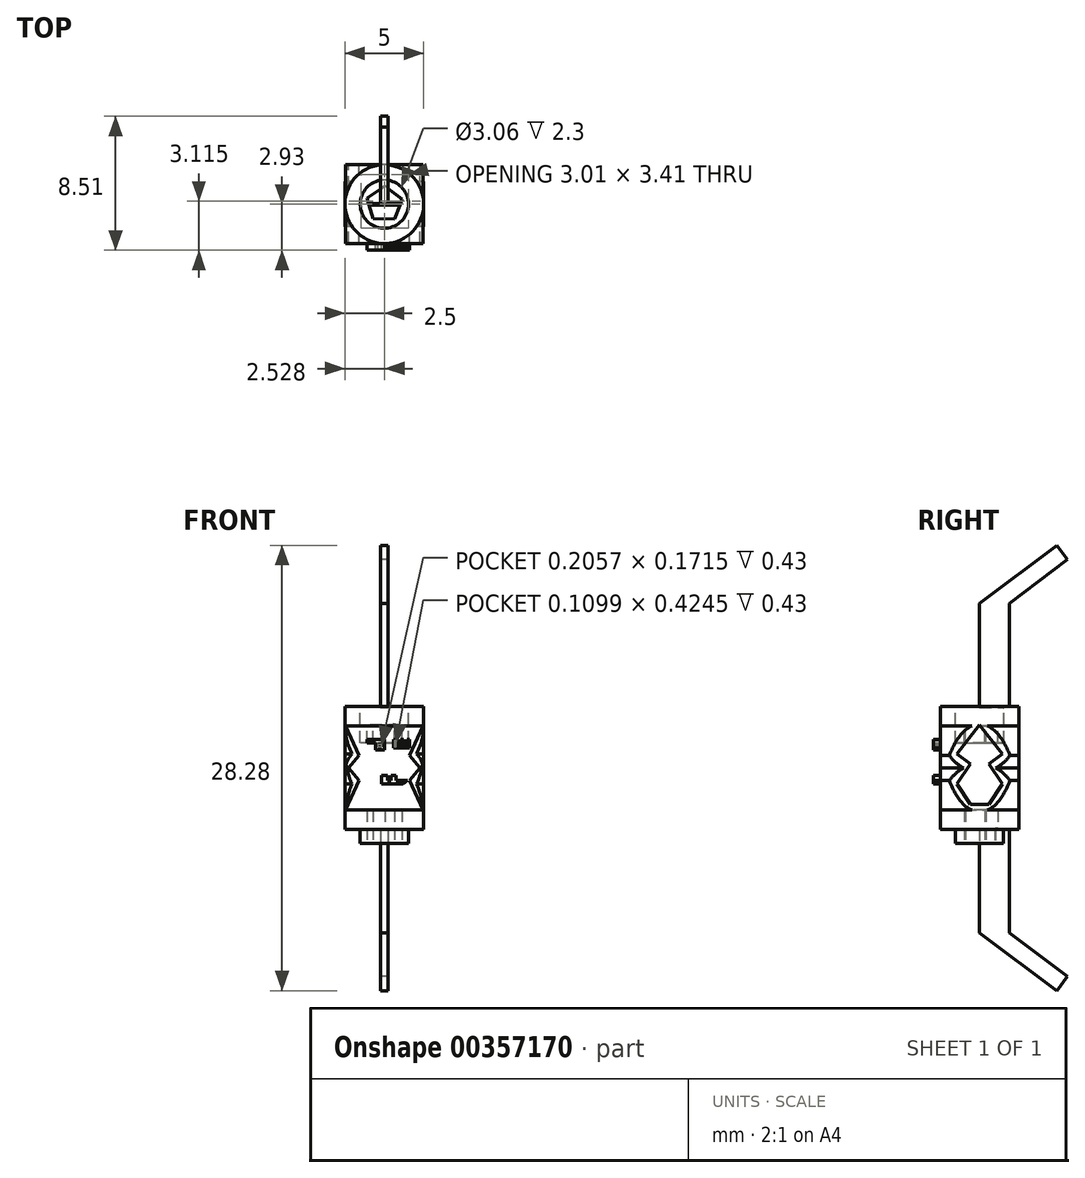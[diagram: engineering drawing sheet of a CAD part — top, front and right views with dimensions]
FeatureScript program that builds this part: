
annotation { "Feature Type Name" : "Feature", "Feature Type Description" : "" }
export const myFeature = defineFeature(function(context is Context, id is Id, definition is map)
    precondition{}
    {
        {
            var Q0;
            Q0=qCreatedBy(makeId("Top.planeOp"),FACE);
            var sketch = newSketch(context, id + "F0", { "sketchPlane" : qUnion([Q0])});
            skCircle(sketch, "E0", {"center": v(0, 0) * mm, "radius": 2.5 * mm});
            skCircle(sketch, "E1", {"center": v(0, 0) * mm, "radius": 1.53 * mm});
            skCircle(sketch, "E2.cCircle", {"center": v(0, 0) * mm, "radius": 0.94 * mm, "construction": true});
            skLineSegment(sketch, "E2.0", {"start": v(1.12, 0.32) * mm, "end": v(0.65, -0.96) * mm});
            skLineSegment(sketch, "E2.1", {"start": v(0.65, -0.96) * mm, "end": v(-0.72, -0.92) * mm});
            skLineSegment(sketch, "E2.2", {"start": v(-0.72, -0.92) * mm, "end": v(-1.1, 0.4) * mm});
            skLineSegment(sketch, "E2.3", {"start": v(-1.1, 0.4) * mm, "end": v(0.04, 1.16) * mm});
            skLineSegment(sketch, "E2.4", {"start": v(0.04, 1.16) * mm, "end": v(1.12, 0.32) * mm});
            skPoint(sketch, "E2.0.midPoint", {"position": v(0.88, -0.32) * mm});
            skSolve(sketch);
        }
        {
            var Q0;
            Q0=makeQuery(id+"F0.imprint","IMPRINT",FACE,{"disambiguationData":[TD([[makeQuery(id+"F0.imprint","IMPRINT",EDGE,{"derivedFrom":sQuery(id+"F0.wireOp",EDGE,"E1")}),1.0]])]});
            extrude(context, id + "F1", {"entities" : qUnion([Q0]), "endBound" : BoundingType.SYMMETRIC, "depth" : 9.6 * mm});
        }
        {
            var Q0;
            Q0=makeQuery(id+"F0.imprint","IMPRINT",FACE,{"disambiguationData":[TD([[makeQuery(id+"F0.imprint","IMPRINT",EDGE,{"derivedFrom":sQuery(id+"F0.wireOp",EDGE,"E0")}),1.0]])]});
            extrude(context, id + "F2", {"entities" : qUnion([Q0]), "operationType" : NewBodyOperationType.ADD, "endBound" : BoundingType.SYMMETRIC, "depth" : 7.8 * mm});
        }
        {
            var Q0;
            Q0=qCreatedBy(makeId("Front.planeOp"),FACE);
            var sketch = newSketch(context, id + "F3", { "sketchPlane" : qUnion([Q0])});
            skLineSegment(sketch, "E3", {"start": v(0, 2.67) * mm, "end": v(2.28, 0) * mm});
            skLineSegment(sketch, "E4", {"start": v(2.28, 0) * mm, "end": v(0, -2.67) * mm});
            skLineSegment(sketch, "E5", {"start": v(1.6, -0.8) * mm, "end": v(2.45, -2.67) * mm});
            skLineSegment(sketch, "E6", {"start": v(2.45, -2.67) * mm, "end": v(0, -2.67) * mm});
            skLineSegment(sketch, "E7.MirrorCS", {"start": v(1.6, 0.8) * mm, "end": v(2.45, 2.67) * mm});
            skLineSegment(sketch, "E8.MirrorCS", {"start": v(2.45, 2.67) * mm, "end": v(0, 2.67) * mm});
            skLineSegment(sketch, "E9", {"start": v(1.6, 0.8) * mm, "end": v(1.6, -0.8) * mm});
            skLineSegment(sketch, "E10.MirrorCS", {"start": v(-2.45, 2.67) * mm, "end": v(0, 2.67) * mm});
            skLineSegment(sketch, "E11.MirrorCS", {"start": v(0, 2.67) * mm, "end": v(-2.28, 0) * mm});
            skLineSegment(sketch, "E12.MirrorCS", {"start": v(-1.6, 0.8) * mm, "end": v(-2.45, 2.67) * mm});
            skLineSegment(sketch, "E13.MirrorCS", {"start": v(-1.6, 0.8) * mm, "end": v(-1.6, -0.8) * mm});
            skLineSegment(sketch, "E14.MirrorCS", {"start": v(-2.28, 0) * mm, "end": v(0, -2.67) * mm});
            skLineSegment(sketch, "E15.MirrorCS", {"start": v(-1.6, -0.8) * mm, "end": v(-2.45, -2.67) * mm});
            skLineSegment(sketch, "E16.MirrorCS", {"start": v(-2.45, -2.67) * mm, "end": v(0, -2.67) * mm});
            skLineSegment(sketch, "E17", {"start": v(1.6, 0) * mm, "end": v(-1.6, 0) * mm});
            skLineSegment(sketch, "E18", {"start": v(0, 2.67) * mm, "end": v(0, -2.67) * mm});
            skSolve(sketch);
        }
        {
            var Q0;
            Q0 = qSketchRegion(id + "F3", true);
            extrude(context, id + "F4", {"entities" : qUnion([Q0]), "operationType" : NewBodyOperationType.ADD, "endBound" : BoundingType.SYMMETRIC, "depth" : 5 * mm});
        }
        {
            var Q0;
            Q0=qCreatedBy(makeId("Right.planeOp"),FACE);
            var sketch = newSketch(context, id + "F5", { "sketchPlane" : qUnion([Q0])});
            skLineSegment(sketch, "E19", {"start": v(0, 2.74) * mm, "end": v(1.44, 0.9) * mm});
            skLineSegment(sketch, "E20", {"start": v(1.44, 0.9) * mm, "end": v(0.6, 0.25) * mm});
            skLineSegment(sketch, "E21", {"start": v(0.6, 0.25) * mm, "end": v(1.44, -1.02) * mm});
            skLineSegment(sketch, "E22", {"start": v(1.44, -1.02) * mm, "end": v(0.6, -2.32) * mm});
            skLineSegment(sketch, "E23.MirrorCS", {"start": v(0, 2.74) * mm, "end": v(-1.44, 0.9) * mm});
            skLineSegment(sketch, "E24.MirrorCS", {"start": v(-1.44, 0.9) * mm, "end": v(-0.6, 0.25) * mm});
            skLineSegment(sketch, "E25.MirrorCS", {"start": v(-0.6, 0.25) * mm, "end": v(-1.44, -1.02) * mm});
            skLineSegment(sketch, "E26.MirrorCS", {"start": v(-1.44, -1.02) * mm, "end": v(-0.6, -2.32) * mm});
            skLineSegment(sketch, "E27", {"start": v(0.6, -2.32) * mm, "end": v(-0.6, -2.32) * mm});
            skSolve(sketch);
        }
        {
            var Q0;
            Q0 = qSketchRegion(id + "F5", true);
            extrude(context, id + "F6", {"entities" : qUnion([Q0]), "operationType" : NewBodyOperationType.ADD, "endBound" : BoundingType.SYMMETRIC, "depth" : 5 * mm});
        }
        {
            var Q0;
            Q0=makeQuery(id+"F1.opExtrude","CAP_FACE",FACE,{"disambiguationData":[OSD([sQuery(id+"F0.wireOp",EDGE,"E1")])],"isStart":false});
            extrude(context, id + "F7", {"entities" : qUnion([Q0]), "operationType" : NewBodyOperationType.REMOVE, "oppositeDirection" : true, "depth" : 3.2 * mm});
        }
        {
            var Q0;
            Q0=makeQuery(id+"F4.opExtrude","CAP_FACE",FACE,{"disambiguationData":[OSD([sQuery(id+"F3.wireOp",EDGE,"E3"),sQuery(id+"F3.wireOp",EDGE,"E4"),sQuery(id+"F3.wireOp",EDGE,"E5"),sQuery(id+"F3.wireOp",EDGE,"E6"),sQuery(id+"F3.wireOp",EDGE,"E7.MirrorCS"),sQuery(id+"F3.wireOp",EDGE,"E8.MirrorCS"),sQuery(id+"F3.wireOp",EDGE,"E10.MirrorCS"),sQuery(id+"F3.wireOp",EDGE,"E11.MirrorCS"),sQuery(id+"F3.wireOp",EDGE,"E12.MirrorCS"),sQuery(id+"F3.wireOp",EDGE,"E14.MirrorCS"),sQuery(id+"F3.wireOp",EDGE,"E15.MirrorCS"),sQuery(id+"F3.wireOp",EDGE,"E16.MirrorCS")])],"isStart":false});
            var sketch = newSketch(context, id + "F8", { "sketchPlane" : qUnion([Q0])});
            skLineSegment(sketch, "E28", {"start": v(-0.18, -1.01) * mm, "end": v(1.18, -1.01) * mm});
            skPoint(sketch, "E28.startSnap0", {"position": v(-0.44, -1.01) * mm});
            skLineSegment(sketch, "E29", {"start": v(-0.18, -1.01) * mm, "end": v(-0.18, -0.46) * mm});
            skLineSegment(sketch, "E30", {"start": v(-0.18, -0.46) * mm, "end": v(0.2, -0.46) * mm});
            skLineSegment(sketch, "E31", {"start": v(0.2, -0.46) * mm, "end": v(0.2, -0.78) * mm});
            skLineSegment(sketch, "E32", {"start": v(0.2, -0.78) * mm, "end": v(0.42, -0.78) * mm});
            skLineSegment(sketch, "E33", {"start": v(0.42, -0.78) * mm, "end": v(0.42, -0.46) * mm});
            skLineSegment(sketch, "E34", {"start": v(0.42, -0.46) * mm, "end": v(0.73, -0.46) * mm});
            skLineSegment(sketch, "E35", {"start": v(0.73, -0.46) * mm, "end": v(0.73, -0.78) * mm});
            skLineSegment(sketch, "E36", {"start": v(0.73, -0.78) * mm, "end": v(1.18, -0.78) * mm});
            skLineSegment(sketch, "E37.bottom", {"start": v(0, 1.8) * mm, "end": v(-1.08, 1.8) * mm});
            skLineSegment(sketch, "E37.left", {"start": v(0, 1.8) * mm, "end": v(0, 1.6) * mm});
            skLineSegment(sketch, "E37.right", {"start": v(-1.08, 1.8) * mm, "end": v(-1.08, 1.6) * mm});
            skLineSegment(sketch, "E38.top", {"start": v(-0.55, 1.15) * mm, "end": v(0, 1.15) * mm});
            skLineSegment(sketch, "E38.left", {"start": v(-0.55, 1.6) * mm, "end": v(-0.55, 1.15) * mm});
            skLineSegment(sketch, "E38.right", {"start": v(0, 1.6) * mm, "end": v(0, 1.15) * mm});
            skLineSegment(sketch, "E39", {"start": v(-1.08, 1.6) * mm, "end": v(-0.55, 1.6) * mm});
            skPoint(sketch, "E40.middle", {"position": v(-0.27, 1.27) * mm});
            skPoint(sketch, "E40.middle.positionSnap0", {"position": v(-0.27, 1.15) * mm});
            skPoint(sketch, "E40.centerSnap0", {"position": v(-0.27, 1.15) * mm});
            skLineSegment(sketch, "E41", {"start": v(-0.94, 1.71) * mm, "end": v(-0.09, 1.71) * mm});
            skLineSegment(sketch, "E42", {"start": v(-0.09, 1.71) * mm, "end": v(-0.09, 1.27) * mm});
            skLineSegment(sketch, "E43", {"start": v(-0.09, 1.27) * mm, "end": v(-0.46, 1.27) * mm});
            skLineSegment(sketch, "E44", {"start": v(-0.46, 1.27) * mm, "end": v(-0.46, 1.6) * mm});
            skLineSegment(sketch, "E45", {"start": v(-0.46, 1.6) * mm, "end": v(-0.18, 1.6) * mm});
            skLineSegment(sketch, "E46", {"start": v(-0.18, 1.6) * mm, "end": v(-0.18, 1.34) * mm});
            skLineSegment(sketch, "E47", {"start": v(-0.18, 1.34) * mm, "end": v(-0.39, 1.34) * mm});
            skLineSegment(sketch, "E48", {"start": v(-0.39, 1.34) * mm, "end": v(-0.39, 1.5) * mm});
            skLineSegment(sketch, "E49", {"start": v(0.6, 1.28) * mm, "end": v(0.6, 1.8) * mm});
            skLineSegment(sketch, "E50", {"start": v(0.6, 1.28) * mm, "end": v(1.23, 1.28) * mm});
            skLineSegment(sketch, "E51", {"start": v(1.23, 1.4) * mm, "end": v(1.23, 1.8) * mm});
            skLineSegment(sketch, "E52", {"start": v(1.23, 1.28) * mm, "end": v(1.6, 1.28) * mm});
            skLineSegment(sketch, "E53", {"start": v(1.6, 1.28) * mm, "end": v(1.6, 1.8) * mm});
            skLineSegment(sketch, "E54", {"start": v(0.6, 1.8) * mm, "end": v(0.81, 1.8) * mm});
            skLineSegment(sketch, "E55", {"start": v(0.81, 1.8) * mm, "end": v(0.81, 1.4) * mm});
            skLineSegment(sketch, "E56", {"start": v(0.81, 1.4) * mm, "end": v(1.04, 1.4) * mm});
            skLineSegment(sketch, "E57", {"start": v(1.04, 1.4) * mm, "end": v(1.04, 1.8) * mm});
            skLineSegment(sketch, "E58", {"start": v(1.04, 1.8) * mm, "end": v(1.23, 1.8) * mm});
            skLineSegment(sketch, "E59", {"start": v(1.6, 1.8) * mm, "end": v(1.44, 1.8) * mm});
            skLineSegment(sketch, "E60", {"start": v(1.44, 1.8) * mm, "end": v(1.44, 1.4) * mm});
            skLineSegment(sketch, "E61", {"start": v(1.44, 1.4) * mm, "end": v(1.23, 1.4) * mm});
            skLineSegment(sketch, "E62", {"start": v(0.82, 1.34) * mm, "end": v(1.53, 1.34) * mm});
            skLineSegment(sketch, "E63", {"start": v(1.53, 1.34) * mm, "end": v(1.53, 1.75) * mm});
            skLineSegment(sketch, "E64.bottom", {"start": v(1.08, 1.8) * mm, "end": v(1.2, 1.8) * mm});
            skLineSegment(sketch, "E64.left", {"start": v(1.08, 1.8) * mm, "end": v(1.08, 1.34) * mm});
            skLineSegment(sketch, "E64.right", {"start": v(1.2, 1.8) * mm, "end": v(1.2, 1.34) * mm});
            skLineSegment(sketch, "E65.bottom", {"start": v(0.76, 1.76) * mm, "end": v(0.65, 1.76) * mm});
            skLineSegment(sketch, "E65.left", {"start": v(0.76, 1.76) * mm, "end": v(0.76, 1.34) * mm});
            skLineSegment(sketch, "E65.right", {"start": v(0.65, 1.76) * mm, "end": v(0.65, 1.34) * mm});
            skLineSegment(sketch, "E66", {"start": v(0.65, 1.34) * mm, "end": v(0.8, 1.34) * mm});
            skLineSegment(sketch, "E67", {"start": v(1.53, 1.75) * mm, "end": v(1.44, 1.75) * mm});
            skLineSegment(sketch, "E68", {"start": v(1.53, 1.75) * mm, "end": v(1.6, 1.75) * mm});
            skLineSegment(sketch, "E69", {"start": v(-0.39, 1.5) * mm, "end": v(-0.18, 1.5) * mm});
            skLineSegment(sketch, "E70", {"start": v(1.18, -1.01) * mm, "end": v(1.47, -0.78) * mm});
            skLineSegment(sketch, "E71", {"start": v(1.18, -0.78) * mm, "end": v(1.47, -0.78) * mm});
            skLineSegment(sketch, "E72", {"start": v(0.76, 1.34) * mm, "end": v(0.76, 1.3) * mm});
            skLineSegment(sketch, "E73", {"start": v(0.76, 1.3) * mm, "end": v(1.3, 1.3) * mm});
            skLineSegment(sketch, "E74", {"start": v(1.3, 1.3) * mm, "end": v(1.54, 1.29) * mm});
            skLineSegment(sketch, "E75", {"start": v(1.54, 1.29) * mm, "end": v(1.57, 1.34) * mm});
            skLineSegment(sketch, "E76", {"start": v(1.57, 1.34) * mm, "end": v(1.57, 1.36) * mm});
            skLineSegment(sketch, "E77", {"start": v(1.57, 1.36) * mm, "end": v(1.57, 1.72) * mm});
            skLineSegment(sketch, "E78", {"start": v(1.57, 1.72) * mm, "end": v(1.57, 1.75) * mm});
            skSolve(sketch);
        }
        {
            var Q0;
            Q0 = qSketchRegion(id + "F8", true);
            extrude(context, id + "F9", {"entities" : qUnion([Q0]), "operationType" : NewBodyOperationType.ADD, "depth" : 0.4 * mm});
        }
        {
            var Q0;
            Q0=qCreatedBy(makeId("Right.planeOp"),FACE);
            var sketch = newSketch(context, id + "F10", { "sketchPlane" : qUnion([Q0])});
            skLineSegment(sketch, "E79", {"start": v(0, 3.86) * mm, "end": v(0, 10.46) * mm});
            skLineSegment(sketch, "E80", {"start": v(0, 10.46) * mm, "end": v(4.9, 14.14) * mm});
            skLineSegment(sketch, "E81", {"start": v(4.9, 14.14) * mm, "end": v(5.58, 13.24) * mm});
            skLineSegment(sketch, "E82", {"start": v(5.58, 13.24) * mm, "end": v(1.89, 10.46) * mm});
            skLineSegment(sketch, "E83", {"start": v(1.89, 10.46) * mm, "end": v(1.89, 3.82) * mm});
            skLineSegment(sketch, "E84", {"start": v(0, 3.86) * mm, "end": v(1.89, 3.82) * mm});
            skLineSegment(sketch, "E85.MirrorCS", {"start": v(0, -3.86) * mm, "end": v(0, -10.46) * mm});
            skLineSegment(sketch, "E86.MirrorCS", {"start": v(1.89, -10.46) * mm, "end": v(1.89, -3.82) * mm});
            skLineSegment(sketch, "E87.MirrorCS", {"start": v(0, -10.46) * mm, "end": v(4.9, -14.14) * mm});
            skLineSegment(sketch, "E88.MirrorCS", {"start": v(5.58, -13.24) * mm, "end": v(1.89, -10.46) * mm});
            skLineSegment(sketch, "E89.MirrorCS", {"start": v(0, -3.86) * mm, "end": v(1.89, -3.82) * mm});
            skLineSegment(sketch, "E90.MirrorCS", {"start": v(4.9, -14.14) * mm, "end": v(5.58, -13.24) * mm});
            skSolve(sketch);
        }
        {
            var Q0;
            Q0 = qSketchRegion(id + "F10", true);
            extrude(context, id + "F11", {"entities" : qUnion([Q0]), "operationType" : NewBodyOperationType.ADD, "endBound" : BoundingType.SYMMETRIC, "depth" : .5 * mm});
        }
        {
            var Q0;
            Q0 = qSketchRegion(id + "F8", true);
            extrude(context, id + "F12", {"entities" : qUnion([Q0]), "operationType" : NewBodyOperationType.ADD, "depth" : 0.43 * mm});
        }
    });
